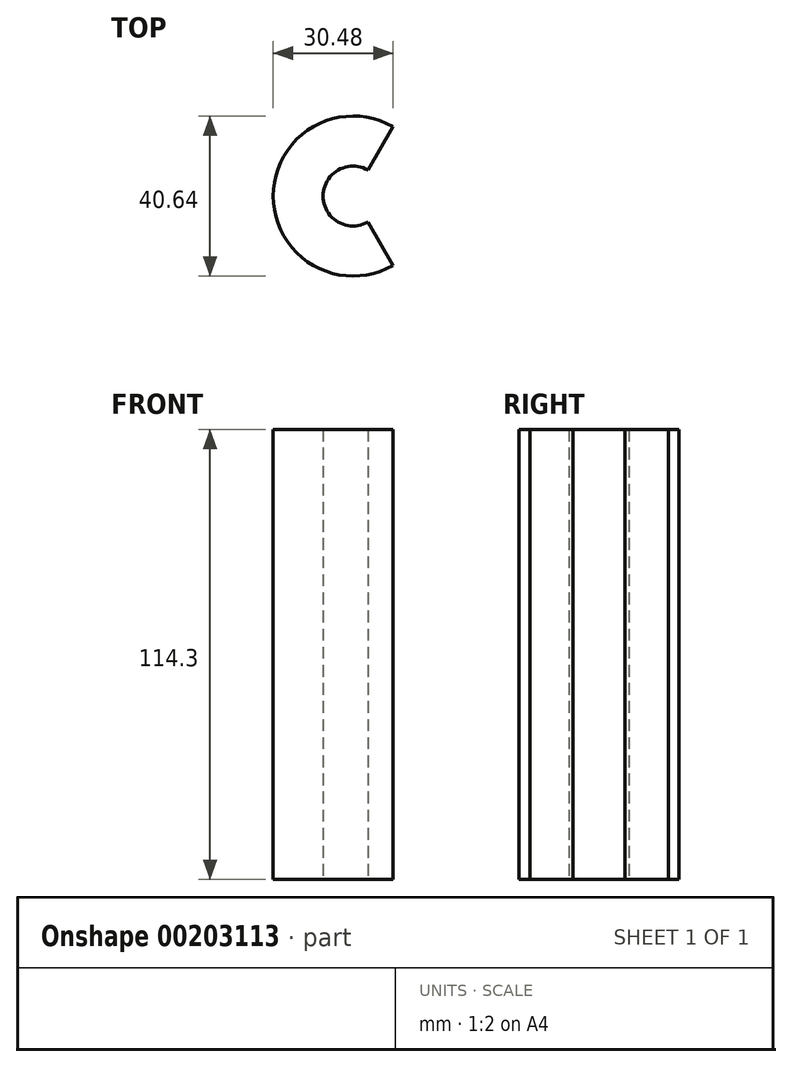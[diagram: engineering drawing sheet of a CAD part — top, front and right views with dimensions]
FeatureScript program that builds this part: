
annotation { "Feature Type Name" : "Feature", "Feature Type Description" : "" }
export const myFeature = defineFeature(function(context is Context, id is Id, definition is map)
    precondition{}
    {
        {
            var Q0;
            Q0=qCreatedBy(makeId("Front.planeOp"),FACE);
            var sketch = newSketch(context, id + "F0", { "sketchPlane" : qUnion([Q0])});
            skLineSegment(sketch, "E0.bottom", {"start": v(-20.32, 45.68) * mm, "end": v(0, 45.68) * mm});
            skLineSegment(sketch, "E0.top", {"start": v(-20.32, -68.62) * mm, "end": v(0, -68.62) * mm});
            skLineSegment(sketch, "E0.left", {"start": v(-20.32, 45.68) * mm, "end": v(-20.32, -68.62) * mm});
            skLineSegment(sketch, "E0.right", {"start": v(0, 45.68) * mm, "end": v(0, -68.62) * mm});
            skText(sketch, "E1", { "text": "Combustibile di Reazione (Idruro di litio)", "fontName": "OpenSans-Regular.ttf"});
            const initialGuessF0  = {"E1": [-0.1126, 0.08376, 1, 0, 0.01075]};
            skSetInitialGuess(sketch, initialGuessF0);
            skSolve(sketch);
        }
        {
            var Q0;
            Q0=makeQuery(id+"F0.imprint","IMPRINT",FACE,{"disambiguationData":[TD([[makeQuery(id+"F0.imprint","IMPRINT",EDGE,{"derivedFrom":sQuery(id+"F0.wireOp",EDGE,"E0.bottom")}),-1.0]])]});
            var Q1;
            Q1=sQuery(id+"F0.wireOp",EDGE,"E0.right");
            revolve(context, id + "F1", {"entities" : qUnion([Q0]), "axis" : qUnion([Q1]), "revolveType" : RevolveType.SYMMETRIC, "angle" : 240 * degree});
        }
        {
            var Q0;
            Q0=qCreatedBy(makeId("Front.planeOp"),FACE);
            var sketch = newSketch(context, id + "F2", { "sketchPlane" : qUnion([Q0])});
            skLineSegment(sketch, "E2.bottom", {"start": v(0, 58.1) * mm, "end": v(-7.62, 58.1) * mm});
            skLineSegment(sketch, "E2.top", {"start": v(0, -68.9) * mm, "end": v(-7.62, -68.9) * mm});
            skLineSegment(sketch, "E2.left", {"start": v(0, 58.1) * mm, "end": v(0, -68.9) * mm});
            skLineSegment(sketch, "E2.right", {"start": v(-7.62, 58.1) * mm, "end": v(-7.62, -68.9) * mm});
            skSolve(sketch);
        }
        {
            var Q0;
            Q0 = qSketchRegion(id + "F2", true);
            var Q1;
            Q1=sQuery(id+"F2.wireOp",EDGE,"E2.left");
            revolve(context, id + "F3", {"operationType" : NewBodyOperationType.REMOVE, "entities" : qUnion([Q0]), "axis" : qUnion([Q1]), "revolveType" : RevolveType.FULL, "oppositeDirection" : true});
        }
    });
